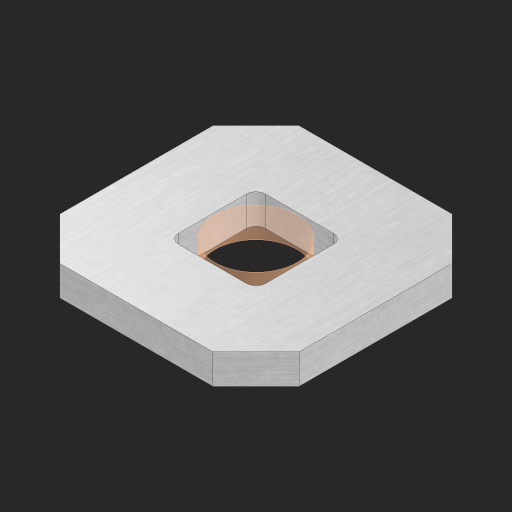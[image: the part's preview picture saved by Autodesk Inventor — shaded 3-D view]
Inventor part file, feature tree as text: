
AUTODESK INVENTOR PART (.ipt)
format: ipt  version: 2023 (Build 270158000, 158)  size: 300,544 bytes
history: native  units: in
note: dims shown in document units (in); Inventor stores cm internally (conversion verified against a paired STEP export)
features: sketch x2, other x2, pattern_linear x1
ambient origin geometry x8: Origin, YZ Plane, XZ Plane, XY Plane, X Axis, Y Axis, Z Axis, Center Point
bodies: Solid1 (feature_tree), Body (feature_tree)
feature tree (5):
  pattern_linear  "Rectangular Pattern1"  Spacing1=0.09in  [1 undecoded]
  sketch  "Sketch1"  dims[d1=0.5in]
  sketch  "Sketch2"  dims[d2=0.182in d3=0.09in d4=0.09in d5=0.09in d6=0.09in d7=0.09in d8=0.09in d9=0.09in d10=0.09in d11=0.02in d13=0.0in d14=0.172in d15=0.0625in d16=0.0in d19=0.5in d22=0.5in]
  other  "Srf1"
  other  "Circle"
note: 1 required parameter value undecoded (feature->parameter linkage not recoverable at this tier; creation-order binding heuristic only, values carry confidence <= 0.55)
